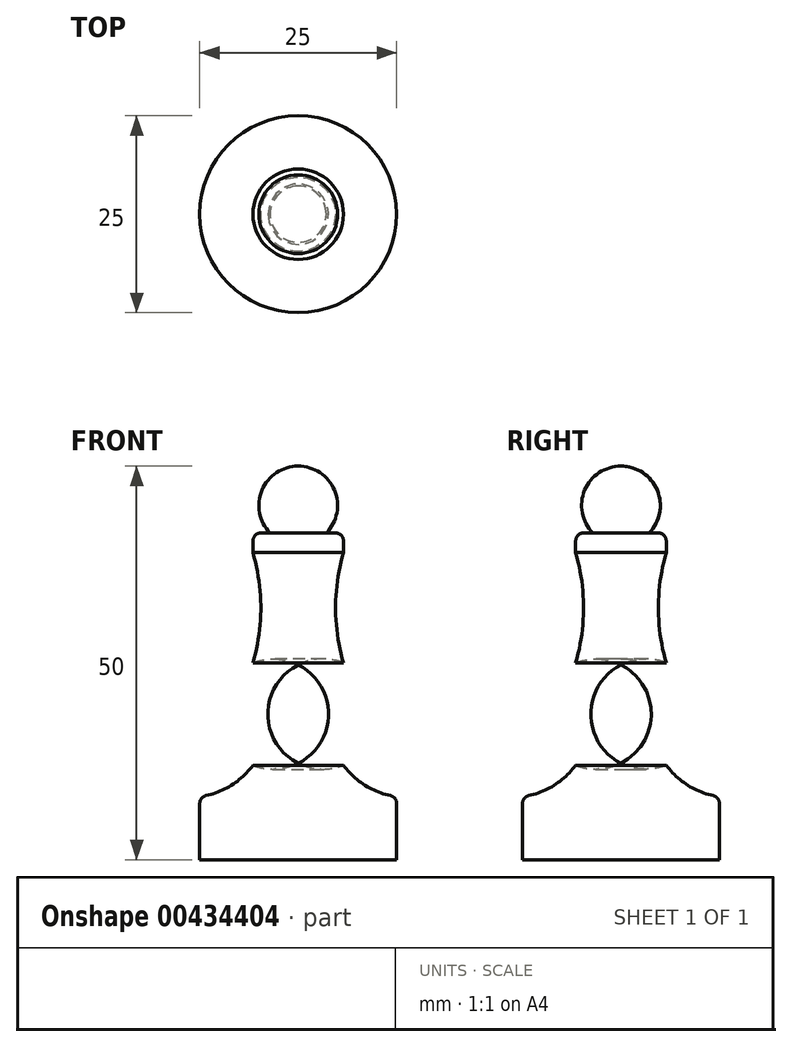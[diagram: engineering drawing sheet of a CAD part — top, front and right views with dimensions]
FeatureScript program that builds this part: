
annotation { "Feature Type Name" : "Feature", "Feature Type Description" : "" }
export const myFeature = defineFeature(function(context is Context, id is Id, definition is map)
    precondition{}
    {
        {
            var Q0;
            Q0=qCreatedBy(makeId("Right.planeOp"),FACE);
            var sketch = newSketch(context, id + "F0", { "sketchPlane" : qUnion([Q0])});
            skLineSegment(sketch, "E0", {"start": v(0, 0) * mm, "end": v(-12.5, 0) * mm});
            skLineSegment(sketch, "E1", {"start": v(-12.5, 0) * mm, "end": v(-12.5, 8) * mm});
            skArc(sketch, "E2", {"start": v(-12.5, 8) * mm, "mid": v(-8.72, 9.31) * mm, "end": v(-5.75, 12) * mm});
            skArc(sketch, "E3", {"start": v(-5.75, 25) * mm, "mid": v(-10.15, 18.5) * mm, "end": v(-5.75, 12) * mm});
            skArc(sketch, "E4", {"start": v(-5.75, 25) * mm, "mid": v(-4.75, 32) * mm, "end": v(-5.75, 39) * mm});
            skLineSegment(sketch, "E5", {"start": v(-5.75, 39) * mm, "end": v(-5.75, 41.5) * mm});
            skLineSegment(sketch, "E6", {"start": v(-5.75, 41.5) * mm, "end": v(-3.57, 41.5) * mm});
            skArc(sketch, "E7", {"start": v(0, 50) * mm, "mid": v(-4.6, 46.94) * mm, "end": v(-3.57, 41.5) * mm});
            skLineSegment(sketch, "E8", {"start": v(0, 50) * mm, "end": v(0, 0) * mm});
            skSolve(sketch);
        }
        {
            var Q0;
            Q0 = qSketchRegion(id + "F0", true);
            var Q1;
            Q1=sQuery(id+"F0.wireOp",EDGE,"E8");
            revolve(context, id + "F1", {"entities" : qUnion([Q0]), "axis" : qUnion([Q1]), "revolveType" : RevolveType.FULL});
        }
        {
            var Q0;
            Q0=makeQuery(id+"F1.opRevolve","SWEPT_EDGE",EDGE,{"disambiguationData":[OSD([sQuery(id+"F0.wireOp",EDGE,"E1"),sQuery(id+"F0.wireOp",EDGE,"E2")])]});
            fillet(context, id + "F2", {"entities" : qUnion([Q0]), "radius" : 1 * mm, "tangentPropagation" : true, "allowEdgeOverflow" : false});
        }
        {
            var Q0;
            Q0=makeQuery(id+"F1.opRevolve","SWEPT_EDGE",EDGE,{"disambiguationData":[OSD([sQuery(id+"F0.wireOp",EDGE,"E5"),sQuery(id+"F0.wireOp",EDGE,"E6")])]});
            fillet(context, id + "F3", {"entities" : qUnion([Q0]), "radius" : 1 * mm, "tangentPropagation" : true, "allowEdgeOverflow" : false});
        }
    });
